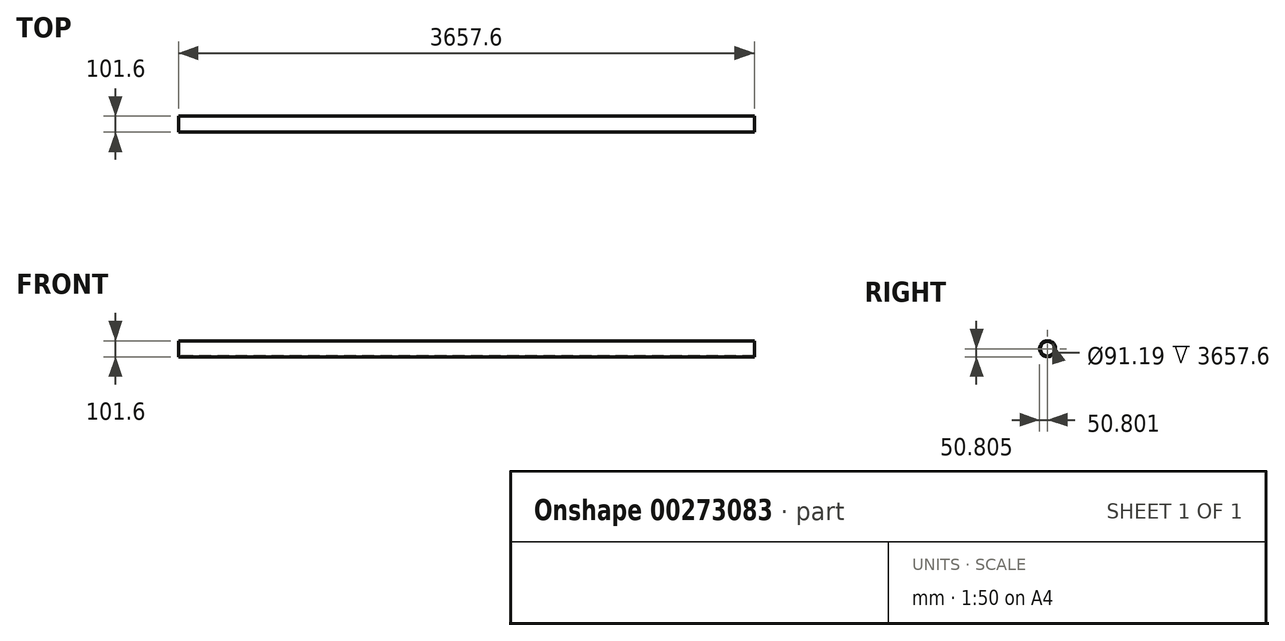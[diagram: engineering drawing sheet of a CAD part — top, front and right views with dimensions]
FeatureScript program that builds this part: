
annotation { "Feature Type Name" : "Feature", "Feature Type Description" : "" }
export const myFeature = defineFeature(function(context is Context, id is Id, definition is map)
    precondition{}
    {
        {
            var Q0;
            Q0=qCreatedBy(makeId("Right.planeOp"),FACE);
            var sketch = newSketch(context, id + "F0", { "sketchPlane" : qUnion([Q0])});
            skCircle(sketch, "E0", {"center": v(-26.78, 18.61) * mm, "radius": 50.8 * mm});
            skCircle(sketch, "E1", {"center": v(-26.78, 18.61) * mm, "radius": 45.6 * mm});
            skSolve(sketch);
        }
        {
            var Q0;
            Q0 = qSketchRegion(id + "F0", true);
            extrude(context, id + "F1", {"entities" : qUnion([Q0]), "depth" : 3657.6 * mm});
        }
    });
